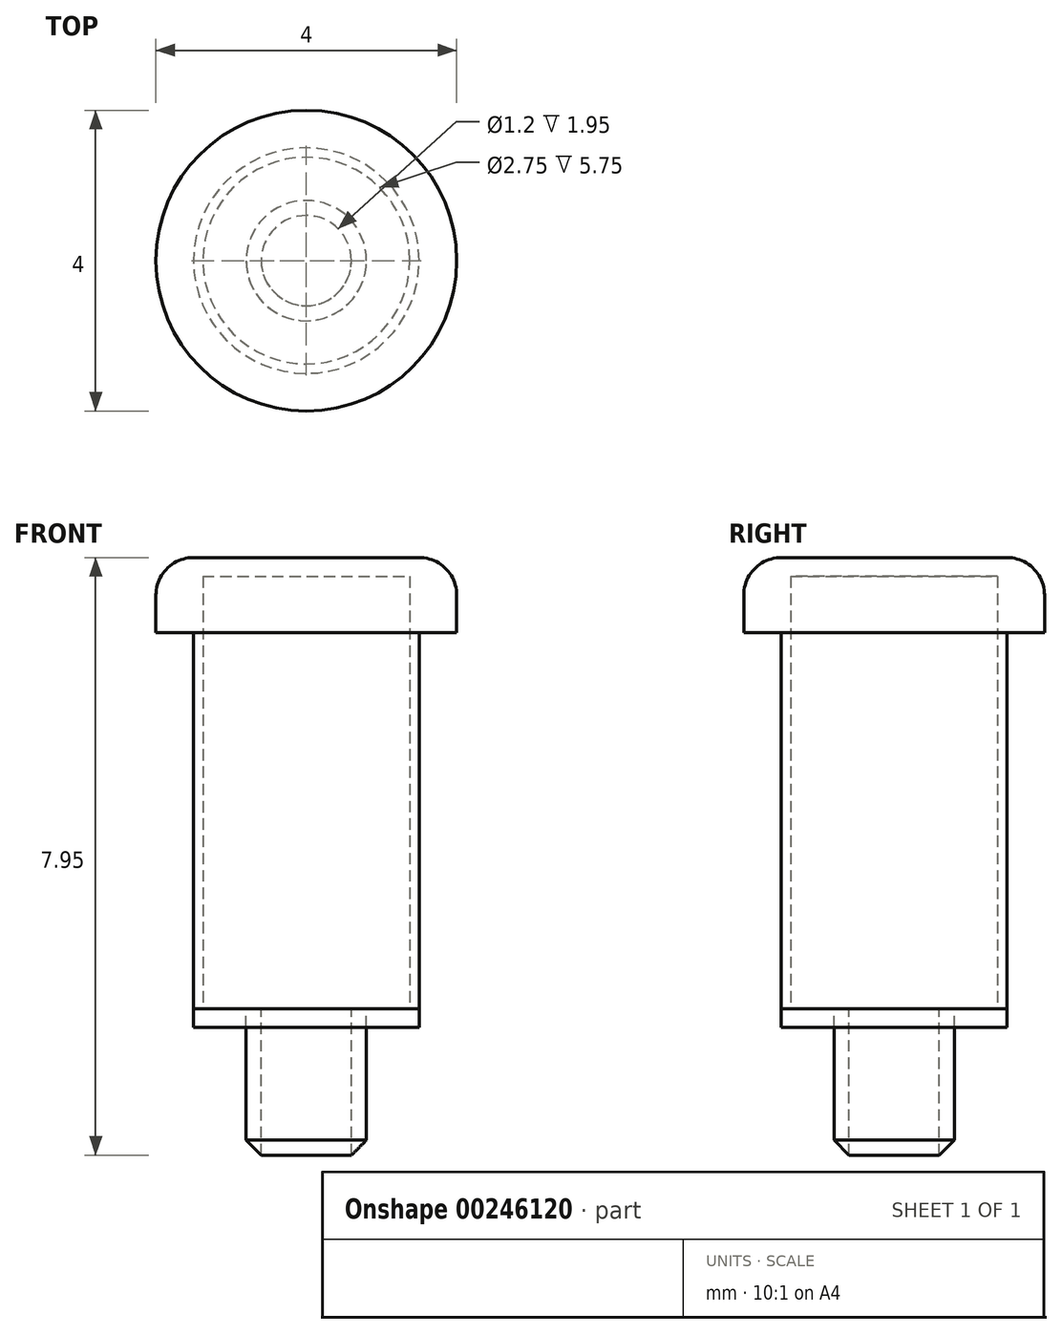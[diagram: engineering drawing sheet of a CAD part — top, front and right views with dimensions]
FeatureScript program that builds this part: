
annotation { "Feature Type Name" : "Feature", "Feature Type Description" : "" }
export const myFeature = defineFeature(function(context is Context, id is Id, definition is map)
    precondition{}
    {
        {
            var Q0;
            Q0=qCreatedBy(makeId("Top.planeOp"),FACE);
            var sketch = newSketch(context, id + "F0", { "sketchPlane" : qUnion([Q0])});
            skCircle(sketch, "E0", {"center": v(0, 0) * mm, "radius": 2 * mm});
            skSolve(sketch);
        }
        {
            var Q0;
            Q0=makeQuery(id+"F0.imprint","IMPRINT",FACE,{"disambiguationData":[TD([[makeQuery(id+"F0.imprint","IMPRINT",EDGE,{"derivedFrom":sQuery(id+"F0.wireOp",EDGE,"E0")}),1.0]])]});
            extrude(context, id + "F1", {"entities" : qUnion([Q0]), "oppositeDirection" : true, "depth" : 6 * mm});
        }
        {
            var Q0;
            Q0=makeQuery(id+"F1.opExtrude","CAP_FACE",FACE,{"disambiguationData":[OSD([sQuery(id+"F0.wireOp",EDGE,"E0")])],"isStart":false});
            var sketch = newSketch(context, id + "F2", { "sketchPlane" : qUnion([Q0])});
            skPoint(sketch, "E1.1", {"position": v(0, 0) * mm});
            skCircle(sketch, "E2", {"center": v(0, 0) * mm, "radius": 2 * mm});
            skCircle(sketch, "E3", {"center": v(0, 0) * mm, "radius": 1.5 * mm});
            skCircle(sketch, "E4", {"center": v(0, 0) * mm, "radius": 1.38 * mm});
            skCircle(sketch, "E5", {"center": v(0, 0) * mm, "radius": 0.8 * mm});
            skCircle(sketch, "E6", {"center": v(0, 0) * mm, "radius": 0.6 * mm});
            skSolve(sketch);
        }
        {
            var Q0;
            Q0=makeQuery(id+"F2.imprint","IMPRINT",FACE,{"disambiguationData":[TD([[makeQuery(id+"F2.imprint","IMPRINT",EDGE,{"derivedFrom":sQuery(id+"F2.wireOp",EDGE,"E2")}),-1.0]])]});
            var Q1;
            Q1=makeQuery(id+"F2.imprint","IMPRINT",FACE,{"disambiguationData":[TD([[makeQuery(id+"F2.imprint","IMPRINT",EDGE,{"derivedFrom":sQuery(id+"F2.wireOp",EDGE,"E4")}),1.0]])]});
            extrude(context, id + "F3", {"entities" : qUnion([Q0, Q1]), "operationType" : NewBodyOperationType.REMOVE, "oppositeDirection" : true, "depth" : 5 * mm});
        }
        {
            var Q0;
            Q0=makeQuery(id+"F1.opExtrude","CAP_EDGE",EDGE,{"disambiguationData":[OSD([sQuery(id+"F0.wireOp",EDGE,"E0")])],"isStart":true});
            var Q1;
            Q1=makeQuery(id+"F3.boolean.opBoolean","COPY",EDGE,{"derivedFrom":makeQuery(id+"F3.opExtrude","CAP_EDGE",EDGE,{"disambiguationData":[OSD([sQuery(id+"F2.wireOp",EDGE,"E2")])],"isStart":false})});
            fillet(context, id + "F4", {"entities" : qUnion([Q0, Q1]), "radius" : .5 * mm, "tangentPropagation" : true, "allowEdgeOverflow" : false});
        }
        {
            var Q0;
            Q0=makeQuery(id+"F2.imprint","IMPRINT",FACE,{"disambiguationData":[TD([[makeQuery(id+"F2.imprint","IMPRINT",EDGE,{"derivedFrom":sQuery(id+"F2.wireOp",EDGE,"E4")}),1.0]])]});
            var Q1;
            Q1=makeQuery(id+"F2.imprint","IMPRINT",FACE,{"disambiguationData":[TD([[makeQuery(id+"F2.imprint","IMPRINT",EDGE,{"derivedFrom":sQuery(id+"F2.wireOp",EDGE,"E3")}),1.0]])]});
            var Q2;
            Q2=sQuery(id+"F2.wireOp",EDGE,"E3");
            extrude(context, id + "F5", {"entities" : qUnion([Q0, Q1]), "surfaceEntities" : qUnion([Q2]), "depth" : .25 * mm});
        }
        {
            var Q0;
            Q0=makeQuery(id+"F2.imprint","IMPRINT",FACE,{"disambiguationData":[TD([[makeQuery(id+"F2.imprint","IMPRINT",EDGE,{"derivedFrom":sQuery(id+"F2.wireOp",EDGE,"E5")}),1.0]])]});
            extrude(context, id + "F6", {"entities" : qUnion([Q0]), "depth" : 2 * mm});
        }
        {
            var Q0;
            Q0=makeQuery(id+"F2.imprint","IMPRINT",FACE,{"disambiguationData":[TD([[makeQuery(id+"F2.imprint","IMPRINT",EDGE,{"derivedFrom":sQuery(id+"F2.wireOp",EDGE,"E4")}),1.0]])]});
            var Q1;
            Q1=makeQuery(id+"F2.imprint","IMPRINT",FACE,{"disambiguationData":[TD([[makeQuery(id+"F2.imprint","IMPRINT",EDGE,{"derivedFrom":sQuery(id+"F2.wireOp",EDGE,"E6")}),1.0]])]});
            var Q2;
            Q2=makeQuery(id+"F2.imprint","IMPRINT",FACE,{"disambiguationData":[TD([[makeQuery(id+"F2.imprint","IMPRINT",EDGE,{"derivedFrom":sQuery(id+"F2.wireOp",EDGE,"E5")}),1.0]])]});
            extrude(context, id + "F7", {"entities" : qUnion([Q0, Q1, Q2]), "operationType" : NewBodyOperationType.REMOVE, "oppositeDirection" : true, "depth" : 5.75 * mm});
        }
        {
            var Q0;
            Q0=makeQuery(id+"F6.opExtrude","CAP_EDGE",EDGE,{"disambiguationData":[OSD([sQuery(id+"F2.wireOp",EDGE,"E5")])],"isStart":false});
            chamfer(context, id + "F8", {"entities" : qUnion([Q0]), "width" : .25 * mm, "tangentPropagation" : true});
        }
    });
